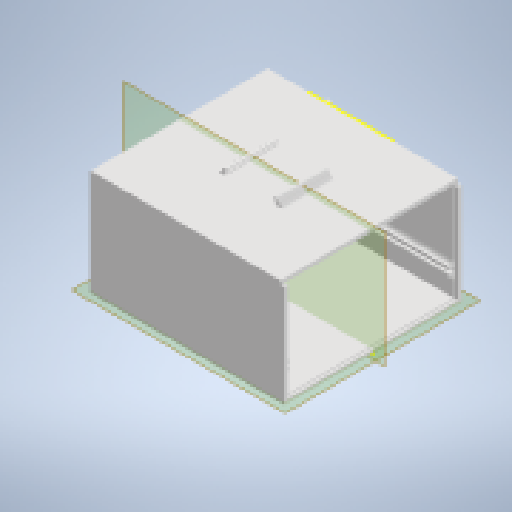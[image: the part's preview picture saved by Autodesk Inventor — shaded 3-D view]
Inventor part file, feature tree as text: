
AUTODESK INVENTOR PART (.ipt)
format: ipt  version: 2023 (Build 270158000, 158)  size: 8,291,328 bytes
history: native  units: mm
features: sketch x25, extrude x21, other x5, fillet x3, projected_geometry x3, sweep x1
ambient origin geometry x8: Origin, YZ Plane, XZ Plane, XY Plane, X Axis, Y Axis, Z Axis, Center Point
bodies: Solide1 (feature_tree)
feature tree (58):
  sketch  "Esquisse1"
  extrude  "Extrusion1"  Depth=133.2mm
  extrude  "Extrusion2"  Depth=146.2mm
  extrude  "Extrusion3"  Depth=3.0mm
  sketch  "Esquisse3"
  extrude  "Extrusion4"  Depth=3.0mm TaperAngle=0.0deg
  extrude  "Extrusion5"  Depth=80.0mm TaperAngle=0.0deg
  extrude  "Extrusion6"  Depth=3.0mm TaperAngle=0.0deg
  extrude  "Extrusion7"  Depth=3.0mm
  extrude  "Extrusion8"  Depth=3.0mm
  fillet  "Congé1"  Radius=3.0mm
  fillet  "Congé2"  Radius=3.0mm
  sketch  "Esquisse9"
  other  "Plan de construction1"
  sketch  "Esquisse11"
  other  "Plan de construction2"
  sweep  "Balayage2"
  sketch  "Esquisse14"
  extrude  "Extrusion9"  Depth=1.0mm
  sketch  "Esquisse15"
  sketch  "Esquisse16"
  extrude  "Extrusion11"  Depth=2.0mm TaperAngle=0.0deg
  extrude  "Extrusion12"  Depth=1.0mm
  sketch  "Esquisse17"
  extrude  "Extrusion13"  Depth=2.0mm TaperAngle=0.0deg
  extrude  "Extrusion14"  Depth=2.0mm TaperAngle=0.0deg
  fillet  "Congé3"  Radius=4.0mm
  extrude  "Extrusion15"  Depth=4.0mm
  extrude  "Extrusion16"  Depth=1.9mm
  extrude  "Extrusion18"  Depth=3.0mm
  sketch  "Esquisse24"
  extrude  "Extrusion19"  Depth=3.0mm
  extrude  "Extrusion20"  Depth=20.0mm
  extrude  "Extrusion21"  Depth=2.0mm TaperAngle=0.0deg
  sketch  "Esquisse26"
  sketch  "Esquisse27"
  extrude  "Extrusion22"  Depth=3.0mm
  extrude  "Extrusion23"  Depth=1.0mm
  sketch  "Esquisse29"
  other  "Gravure1"
  other  "Gravure2"
  other  "Gravure3"
  sketch  "Esquisse2"
  sketch  "Esquisse4"
  sketch  "Esquisse5"
  sketch  "Esquisse6"
  sketch  "Esquisse7"
  sketch  "Esquisse8"
  sketch  "Esquisse13"
  sketch  "Esquisse19"
  sketch  "Esquisse20"
  sketch  "Esquisse21"
  sketch  "Esquisse23"
  sketch  "Esquisse25"
  projected_geometry  "Boucle projetée2"
  projected_geometry  "Boucle projetée3"
  projected_geometry  "Boucle projetée4"
  sketch  "Esquisse30"
